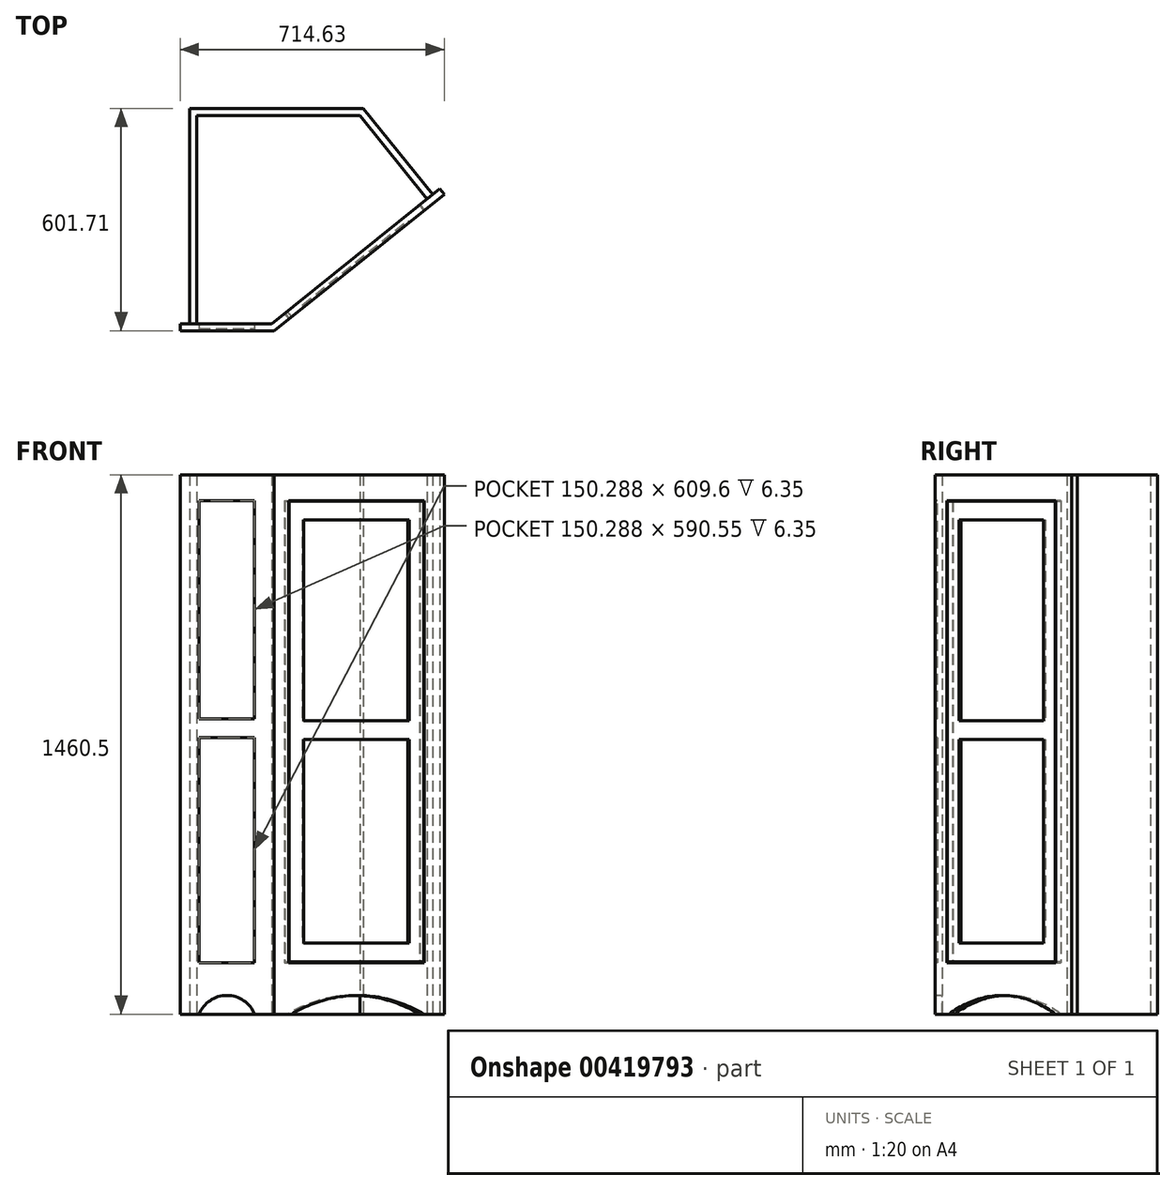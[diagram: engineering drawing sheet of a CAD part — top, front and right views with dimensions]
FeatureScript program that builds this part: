
annotation { "Feature Type Name" : "Feature", "Feature Type Description" : "" }
export const myFeature = defineFeature(function(context is Context, id is Id, definition is map)
    precondition{}
    {
        {
            var Q0;
            Q0=qCreatedBy(makeId("Top.planeOp"),FACE);
            var sketch = newSketch(context, id + "F0", { "sketchPlane" : qUnion([Q0])});
            skLineSegment(sketch, "E0", {"start": v(0, 0) * mm, "end": v(0, -627.1) * mm, "construction": true});
            skLineSegment(sketch, "E1", {"start": v(0, -627.1) * mm, "end": v(254, -627.1) * mm});
            skLineSegment(sketch, "E2", {"start": v(0, 0) * mm, "end": v(508, 0) * mm, "construction": true});
            skLineSegment(sketch, "E3", {"start": v(508, 0) * mm, "end": v(714.63, -257.56) * mm, "construction": true});
            skLineSegment(sketch, "E4", {"start": v(508, 0) * mm, "end": v(950.47, 0) * mm});
            skLineSegment(sketch, "E5", {"start": v(714.63, -257.56) * mm, "end": v(254, -627.1) * mm});
            skLineSegment(sketch, "E6.0", {"start": v(19.05, -608.06) * mm, "end": v(247.3, -608.06) * mm});
            skLineSegment(sketch, "E6.1", {"start": v(687.85, -254.62) * mm, "end": v(247.3, -608.06) * mm});
            skLineSegment(sketch, "E7", {"start": v(19.05, -608.06) * mm, "end": v(0, -608.06) * mm});
            skLineSegment(sketch, "E8", {"start": v(687.85, -254.62) * mm, "end": v(702.7, -242.7) * mm});
            skLineSegment(sketch, "E9.0", {"start": v(25.4, -25.4) * mm, "end": v(25.4, -608.06) * mm});
            skLineSegment(sketch, "E9.1", {"start": v(25.4, -25.4) * mm, "end": v(495.81, -25.4) * mm});
            skLineSegment(sketch, "E9.2", {"start": v(495.81, -25.4) * mm, "end": v(682.9, -258.6) * mm});
            skLineSegment(sketch, "E10.0", {"start": v(44.45, -44.45) * mm, "end": v(44.45, -608.06) * mm});
            skLineSegment(sketch, "E10.1", {"start": v(44.45, -44.45) * mm, "end": v(486.67, -44.45) * mm});
            skLineSegment(sketch, "E10.2", {"start": v(486.67, -44.45) * mm, "end": v(668.04, -270.51) * mm});
            skLineSegment(sketch, "E11", {"start": v(486.67, -44.45) * mm, "end": v(495.81, -25.4) * mm});
            skLineSegment(sketch, "E12", {"start": v(44.45, -44.45) * mm, "end": v(25.4, -44.45) * mm});
            skLineSegment(sketch, "E13", {"start": v(0, -627.1) * mm, "end": v(0, -608.06) * mm});
            skLineSegment(sketch, "E14", {"start": v(247.3, -608.06) * mm, "end": v(254, -627.1) * mm});
            skLineSegment(sketch, "E15", {"start": v(714.63, -257.56) * mm, "end": v(702.7, -242.7) * mm});
            skSolve(sketch);
        }
        {
            var Q0;
            {var subQ3=sQuery(id+"F0.wireOp",EDGE,"E10.0");Q0=makeQuery(id+"F0.imprint","IMPRINT",FACE,{"disambiguationData":[TD([[makeQuery(id+"F0.imprint","IMPRINT",EDGE,{"derivedFrom":subQ3}),-1.0]])]});}
            var Q1;
            {var subQ0=sQuery(id+"F0.wireOp",EDGE,"E9.1");Q1=makeQuery(id+"F0.imprint","IMPRINT",FACE,{"disambiguationData":[TD([[makeQuery(id+"F0.imprint","IMPRINT",EDGE,{"derivedFrom":subQ0}),-1.0]])]});}
            var Q2;
            {var subQ0=sQuery(id+"F0.wireOp",EDGE,"E9.2");Q2=makeQuery(id+"F0.imprint","IMPRINT",FACE,{"disambiguationData":[TD([[makeQuery(id+"F0.imprint","IMPRINT",EDGE,{"derivedFrom":subQ0}),-1.0]])]});}
            extrude(context, id + "F1", {"entities" : qUnion([Q0, Q1, Q2]), "depth" : 1460.5 * mm});
        }
        {
            var Q0;
            Q0=makeQuery(id+"F0.imprint","IMPRINT",FACE,{"disambiguationData":[TD([[makeQuery(id+"F0.imprint","IMPRINT",EDGE,{"derivedFrom":sQuery(id+"F0.wireOp",EDGE,"E1")}),1.0]])]});
            var Q1;
            Q1=makeQuery(id+"F0.imprint","IMPRINT",FACE,{"disambiguationData":[TD([[makeQuery(id+"F0.imprint","IMPRINT",EDGE,{"derivedFrom":sQuery(id+"F0.wireOp",EDGE,"E5")}),-1.0]])]});
            extrude(context, id + "F2", {"entities" : qUnion([Q0, Q1]), "depth" : 1460.5 * mm});
        }
        {
            var Q0;
            Q0=makeQuery(id+"F2.opExtrude","SWEPT_FACE",FACE,{"disambiguationData":[OSD([sQuery(id+"F0.wireOp",EDGE,"E1")])]});
            var sketch = newSketch(context, id + "F3", { "sketchPlane" : qUnion([Q0])});
            skLineSegment(sketch, "E16", {"start": v(0, 0) * mm, "end": v(0, 88.9) * mm});
            skLineSegment(sketch, "E17", {"start": v(50.8, 88.9) * mm, "end": v(201.09, 88.9) * mm});
            skLineSegment(sketch, "E18", {"start": v(0, 88.9) * mm, "end": v(0, 139.7) * mm});
            skLineSegment(sketch, "E19", {"start": v(50.8, 139.7) * mm, "end": v(201.09, 139.7) * mm});
            skLineSegment(sketch, "E20", {"start": v(254, 139.7) * mm, "end": v(254, 0) * mm});
            skLineSegment(sketch, "E21", {"start": v(254, 0) * mm, "end": v(254, 1460.5) * mm});
            skLineSegment(sketch, "E22", {"start": v(254, 1460.5) * mm, "end": v(0, 1460.5) * mm});
            skLineSegment(sketch, "E23", {"start": v(0, 1460.5) * mm, "end": v(0, 139.7) * mm});
            skLineSegment(sketch, "E24.0", {"start": v(50.8, 1390.65) * mm, "end": v(50.8, 0) * mm});
            skLineSegment(sketch, "E24.1", {"start": v(201.09, 1390.65) * mm, "end": v(50.8, 1390.65) * mm});
            skLineSegment(sketch, "E25.trimOffspring", {"start": v(201.09, 0) * mm, "end": v(201.09, 1390.65) * mm});
            skLineSegment(sketch, "E26", {"start": v(254, 0) * mm, "end": v(0, 0) * mm});
            skPoint(sketch, "E27.orphan", {"position": v(254, 88.9) * mm});
            skArc(sketch, "E28", {"start": v(201.09, 0) * mm, "mid": v(125.94, 50.8) * mm, "end": v(50.8, 0) * mm});
            skLineSegment(sketch, "E29", {"start": v(201.09, 1390.65) * mm, "end": v(201.09, 1460.5) * mm});
            skLineSegment(sketch, "E30", {"start": v(50.8, 1390.65) * mm, "end": v(50.8, 1460.5) * mm});
            skLineSegment(sketch, "E31", {"start": v(201.09, 800.1) * mm, "end": v(201.09, 749.3) * mm});
            skLineSegment(sketch, "E32", {"start": v(201.09, 749.3) * mm, "end": v(50.8, 749.3) * mm});
            skLineSegment(sketch, "E33", {"start": v(201.09, 800.1) * mm, "end": v(50.8, 800.1) * mm});
            skSolve(sketch);
        }
        {
            var Q0;
            {var subQ0=sQuery(id+"F3.wireOp",EDGE,"E24.1");Q0=makeQuery(id+"F3.imprint","IMPRINT",FACE,{"disambiguationData":[TD([[makeQuery(id+"F3.imprint","IMPRINT",EDGE,{"derivedFrom":subQ0}),1.0]])]});}
            var Q1;
            {var subQ0=sQuery(id+"F3.wireOp",EDGE,"E19");Q1=makeQuery(id+"F3.imprint","IMPRINT",FACE,{"disambiguationData":[TD([[makeQuery(id+"F3.imprint","IMPRINT",EDGE,{"derivedFrom":subQ0}),1.0]])]});}
            extrude(context, id + "F4", {"entities" : qUnion([Q0, Q1]), "operationType" : NewBodyOperationType.REMOVE, "oppositeDirection" : true, "depth" : 6.35 * mm});
        }
        {
            var Q0;
            {var subQ0=sQuery(id+"F3.wireOp",EDGE,"E28");Q0=makeQuery(id+"F3.imprint","IMPRINT",FACE,{"disambiguationData":[TD([[makeQuery(id+"F3.imprint","IMPRINT",EDGE,{"derivedFrom":subQ0}),1.0]])]});}
            extrude(context, id + "F5", {"entities" : qUnion([Q0]), "operationType" : NewBodyOperationType.REMOVE, "endBound" : BoundingType.UP_TO_NEXT, "oppositeDirection" : true, "depth" : 25.4 * mm});
        }
        {
            var Q0;
            Q0=makeQuery(id+"F2.opExtrude","SWEPT_FACE",FACE,{"disambiguationData":[OSD([sQuery(id+"F0.wireOp",EDGE,"E5")])]});
            var sketch = newSketch(context, id + "F6", { "sketchPlane" : qUnion([Q0])});
            skLineSegment(sketch, "E34.bottom", {"start": v(-194.3, 1460.5) * mm, "end": v(396.24, 1460.5) * mm});
            skLineSegment(sketch, "E34.top", {"start": v(-194.3, 0) * mm, "end": v(396.24, 0) * mm});
            skLineSegment(sketch, "E34.left", {"start": v(-194.3, 1460.5) * mm, "end": v(-194.3, 0) * mm});
            skLineSegment(sketch, "E34.right", {"start": v(396.24, 1460.5) * mm, "end": v(396.24, 0) * mm});
            skLineSegment(sketch, "E35", {"start": v(396.24, 1460.5) * mm, "end": v(326.4, 1460.5) * mm});
            skLineSegment(sketch, "E36", {"start": v(326.4, 1460.5) * mm, "end": v(326.4, 0) * mm});
            skLineSegment(sketch, "E37.0", {"start": v(-143.5, 1460.5) * mm, "end": v(-143.5, -4.12) * mm});
            skLineSegment(sketch, "E38", {"start": v(-143.5, 139.7) * mm, "end": v(326.4, 139.7) * mm});
            skArc(sketch, "E39", {"start": v(326.4, 0) * mm, "mid": v(90.98, 50.78) * mm, "end": v(-143.5, -4.12) * mm});
            skLineSegment(sketch, "E40", {"start": v(326.4, 1390.65) * mm, "end": v(-143.5, 1390.65) * mm});
            skLineSegment(sketch, "E41", {"start": v(-143.5, 84.78) * mm, "end": v(326.4, 84.78) * mm});
            skSolve(sketch);
        }
        {
            var Q0;
            {var subQ0=sQuery(id+"F6.wireOp",EDGE,"E38");Q0=makeQuery(id+"F6.imprint","IMPRINT",FACE,{"disambiguationData":[TD([[makeQuery(id+"F6.imprint","IMPRINT",EDGE,{"derivedFrom":subQ0}),1.0]])]});}
            extrude(context, id + "F7", {"entities" : qUnion([Q0]), "operationType" : NewBodyOperationType.REMOVE, "oppositeDirection" : true, "depth" : 25.4 * mm});
        }
        {
            var Q0;
            Q0=makeQuery(id+"F2.opExtrude","SWEPT_FACE",FACE,{"disambiguationData":[OSD([sQuery(id+"F0.wireOp",EDGE,"E5")])]});
            var sketch = newSketch(context, id + "F8", { "sketchPlane" : qUnion([Q0])});
            skLineSegment(sketch, "E42.bottom", {"start": v(-143.5, 1390.65) * mm, "end": v(326.4, 1390.65) * mm, "construction": true});
            skLineSegment(sketch, "E42.top", {"start": v(-143.5, 139.7) * mm, "end": v(326.4, 139.7) * mm, "construction": true});
            skLineSegment(sketch, "E42.left", {"start": v(-143.5, 1390.65) * mm, "end": v(-143.5, 139.7) * mm, "construction": true});
            skLineSegment(sketch, "E42.right", {"start": v(326.4, 1390.65) * mm, "end": v(326.4, 139.7) * mm, "construction": true});
            skLineSegment(sketch, "E43.0", {"start": v(-141.92, 1389.06) * mm, "end": v(324.8, 1389.06) * mm});
            skLineSegment(sketch, "E43.1", {"start": v(-141.92, 1389.06) * mm, "end": v(-141.92, 141.29) * mm});
            skLineSegment(sketch, "E43.2", {"start": v(-141.92, 141.29) * mm, "end": v(324.8, 141.29) * mm});
            skLineSegment(sketch, "E43.3", {"start": v(324.8, 1389.06) * mm, "end": v(324.8, 141.29) * mm});
            skLineSegment(sketch, "E44.0", {"start": v(-91.12, 1338.26) * mm, "end": v(274, 1338.26) * mm});
            skLineSegment(sketch, "E44.1", {"start": v(-91.12, 1338.26) * mm, "end": v(-91.12, 192.09) * mm});
            skLineSegment(sketch, "E44.2", {"start": v(-91.12, 192.09) * mm, "end": v(274, 192.09) * mm});
            skLineSegment(sketch, "E44.3", {"start": v(274, 1338.26) * mm, "end": v(274, 192.09) * mm});
            skLineSegment(sketch, "E45", {"start": v(-91.12, 794.76) * mm, "end": v(274, 794.76) * mm});
            skLineSegment(sketch, "E46", {"start": v(-91.12, 743.96) * mm, "end": v(274, 743.96) * mm});
            skSolve(sketch);
        }
        {
            var Q0;
            Q0=makeQuery(id+"F8.imprint","IMPRINT",FACE,{"disambiguationData":[TD([[makeQuery(id+"F8.imprint","IMPRINT",EDGE,{"derivedFrom":sQuery(id+"F8.wireOp",EDGE,"E43.0")}),-1.0]])]});
            var Q1;
            {var subQ0=sQuery(id+"F8.wireOp",EDGE,"E45");Q1=makeQuery(id+"F8.imprint","IMPRINT",FACE,{"disambiguationData":[TD([[makeQuery(id+"F8.imprint","IMPRINT",EDGE,{"derivedFrom":subQ0}),-1.0]])]});}
            var Q2;
            {var subQ0=sQuery(id+"F8.wireOp",EDGE,"E44.0");Q2=makeQuery(id+"F8.imprint","IMPRINT",FACE,{"disambiguationData":[TD([[makeQuery(id+"F8.imprint","IMPRINT",EDGE,{"derivedFrom":subQ0}),-1.0]])]});}
            var Q3;
            {var subQ0=sQuery(id+"F8.wireOp",EDGE,"E44.2");Q3=makeQuery(id+"F8.imprint","IMPRINT",FACE,{"disambiguationData":[TD([[makeQuery(id+"F8.imprint","IMPRINT",EDGE,{"derivedFrom":subQ0}),1.0]])]});}
            extrude(context, id + "F9", {"entities" : qUnion([Q0, Q1, Q2, Q3]), "oppositeDirection" : true, "depth" : 19.05 * mm});
        }
        {
            var Q0;
            {var subQ0=sQuery(id+"F8.wireOp",EDGE,"E44.0");Q0=makeQuery(id+"F8.imprint","IMPRINT",FACE,{"disambiguationData":[TD([[makeQuery(id+"F8.imprint","IMPRINT",EDGE,{"derivedFrom":subQ0}),-1.0]])]});}
            var Q1;
            {var subQ0=sQuery(id+"F8.wireOp",EDGE,"E44.2");Q1=makeQuery(id+"F8.imprint","IMPRINT",FACE,{"disambiguationData":[TD([[makeQuery(id+"F8.imprint","IMPRINT",EDGE,{"derivedFrom":subQ0}),1.0]])]});}
            extrude(context, id + "F10", {"entities" : qUnion([Q0, Q1]), "operationType" : NewBodyOperationType.REMOVE, "oppositeDirection" : true, "depth" : 6.35 * mm});
        }
        {
            var Q0;
            {var subQ0=sQuery(id+"F6.wireOp",EDGE,"E39");var subQ1=sQuery(id+"F6.wireOp",EDGE,"E34.top");var subQ3=makeQuery(id+"F6.imprint","INTERSECT",VERTEX,{"derivedFrom":[subQ1,subQ0]});Q0=makeQuery(id+"F6.imprint","IMPRINT",FACE,{"disambiguationData":[TD([[makeQuery(id+"F6.imprint","IMPRINT",EDGE,{"disambiguationData":[TD([[subQ3,1.0]])],"derivedFrom":subQ1}),-1.0]])]});}
            extrude(context, id + "F11", {"entities" : qUnion([Q0]), "operationType" : NewBodyOperationType.REMOVE, "oppositeDirection" : true, "depth" : 25.4 * mm});
        }
    });
